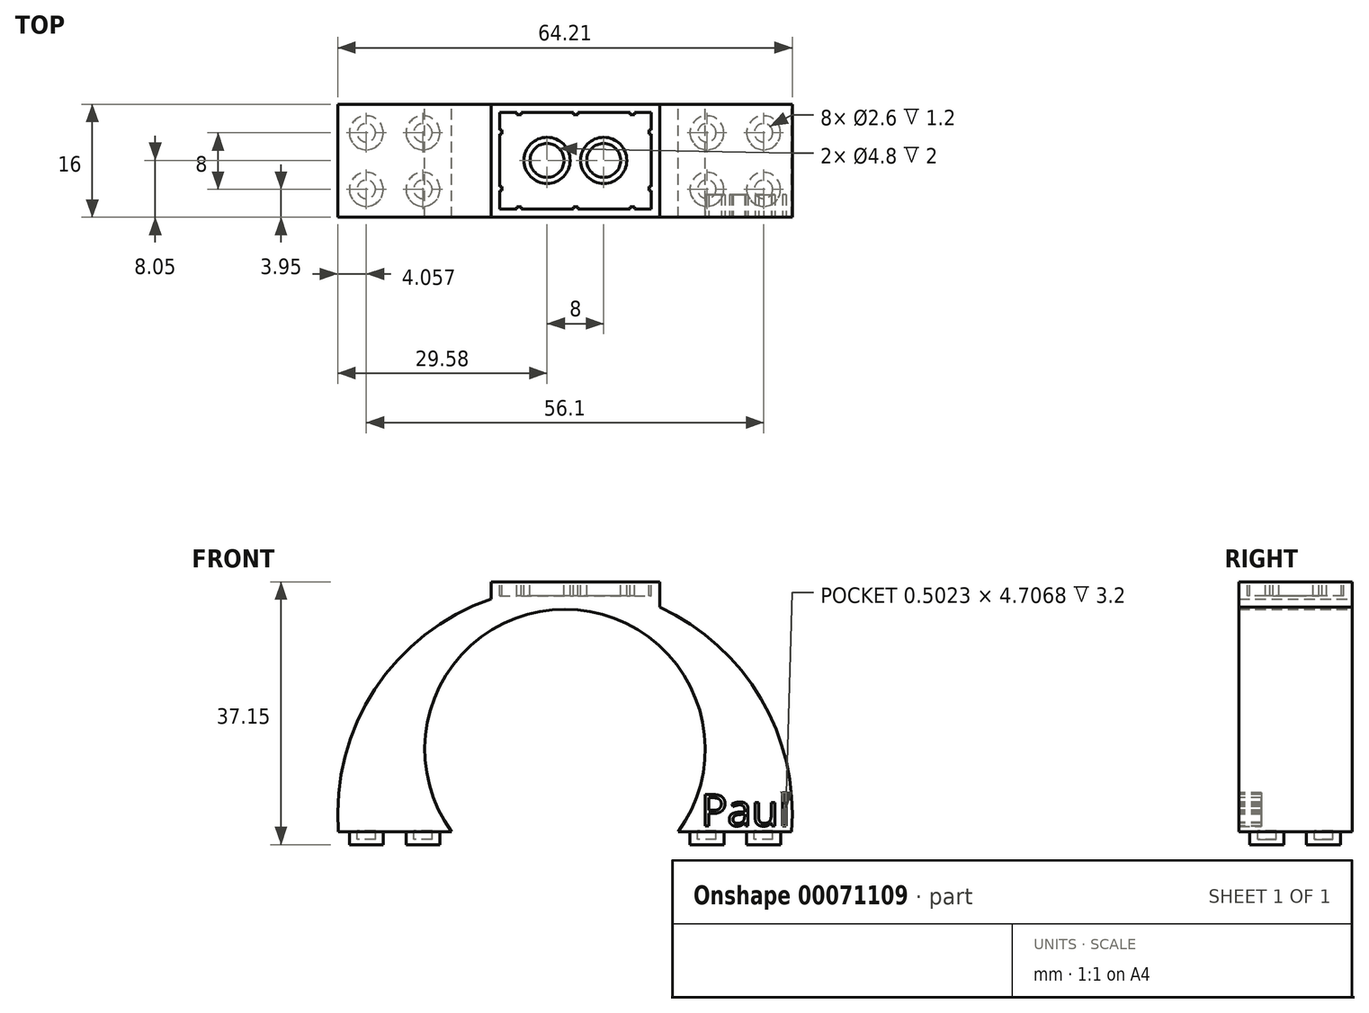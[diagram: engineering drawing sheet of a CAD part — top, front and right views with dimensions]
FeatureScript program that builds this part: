
annotation { "Feature Type Name" : "Feature", "Feature Type Description" : "" }
export const myFeature = defineFeature(function(context is Context, id is Id, definition is map)
    precondition{}
    {
        {
            var Q0;
            Q0=qCreatedBy(makeId("Front.planeOp"),FACE);
            var sketch = newSketch(context, id + "F0", { "sketchPlane" : qUnion([Q0])});
            skLineSegment(sketch, "E0.bottom", {"start": v(-33.47, 63.85) * mm, "end": v(30.53, 63.85) * mm, "construction": true});
            skLineSegment(sketch, "E0.top", {"start": v(-33.47, -0.15) * mm, "end": v(30.53, -0.15) * mm, "construction": true});
            skLineSegment(sketch, "E0.left", {"start": v(-33.47, 63.85) * mm, "end": v(-33.47, -0.15) * mm, "construction": true});
            skLineSegment(sketch, "E0.right", {"start": v(30.53, 63.85) * mm, "end": v(30.53, -0.15) * mm, "construction": true});
            skArc(sketch, "E1", {"start": v(14.53, -0.15) * mm, "mid": v(-1.47, 31.32) * mm, "end": v(-17.47, -0.15) * mm});
            skLineSegment(sketch, "E2", {"start": v(-33.47, -0.15) * mm, "end": v(-17.47, -0.15) * mm});
            skLineSegment(sketch, "E3", {"start": v(14.53, -0.15) * mm, "end": v(30.53, -0.15) * mm});
            skArc(sketch, "E4", {"start": v(30.53, -0.15) * mm, "mid": v(-1.47, 34.52) * mm, "end": v(-33.47, -0.15) * mm});
            skSolve(sketch);
        }
        {
            var Q0;
            Q0 = qSketchRegion(id + "F0", true);
            extrude(context, id + "F1", {"entities" : qUnion([Q0]), "depth" : 16 * mm});
        }
        {
            var Q0;
            Q0=makeQuery(id+"F1.opExtrude","SWEPT_FACE",FACE,{"disambiguationData":[OSD([sQuery(id+"F0.wireOp",EDGE,"E2")])]});
            var sketch = newSketch(context, id + "F2", { "sketchPlane" : qUnion([Q0])});
            skLineSegment(sketch, "E5", {"start": v(-45.71, 8) * mm, "end": v(-17.47, 8) * mm, "construction": true});
            skPoint(sketch, "E5.startSnap0", {"position": v(-17.47, 8) * mm});
            skCircle(sketch, "E6", {"center": v(-29.52, 12.05) * mm, "radius": 2.4 * mm});
            skCircle(sketch, "E7.0.1.0", {"center": v(-29.52, 4.05) * mm, "radius": 2.4 * mm});
            skCircle(sketch, "E7.1.0.0", {"center": v(-21.52, 12.05) * mm, "radius": 2.4 * mm});
            skCircle(sketch, "E7.1.1.0", {"center": v(-21.52, 4.05) * mm, "radius": 2.4 * mm});
            skLineSegment(sketch, "E7.direction1", {"start": v(-29.52, 12.05) * mm, "end": v(-21.52, 12.05) * mm, "construction": true});
            skLineSegment(sketch, "E7.direction2", {"start": v(-29.52, 12.05) * mm, "end": v(-29.52, 4.05) * mm, "construction": true});
            skLineSegment(sketch, "E8", {"start": v(-17.47, 8) * mm, "end": v(43.86, 8) * mm, "construction": true});
            skCircle(sketch, "E9", {"center": v(26.58, 12.05) * mm, "radius": 2.4 * mm});
            skCircle(sketch, "E10.0.1.0", {"center": v(26.58, 4.05) * mm, "radius": 2.4 * mm});
            skCircle(sketch, "E10.1.0.0", {"center": v(18.58, 12.05) * mm, "radius": 2.4 * mm});
            skCircle(sketch, "E10.1.1.0", {"center": v(18.58, 4.05) * mm, "radius": 2.4 * mm});
            skLineSegment(sketch, "E10.direction1", {"start": v(26.58, 12.05) * mm, "end": v(18.58, 12.05) * mm, "construction": true});
            skLineSegment(sketch, "E10.direction2", {"start": v(26.58, 12.05) * mm, "end": v(26.58, 4.05) * mm, "construction": true});
            skSolve(sketch);
        }
        {
            var Q0;
            Q0 = qSketchRegion(id + "F2", true);
            extrude(context, id + "F3", {"entities" : qUnion([Q0]), "operationType" : NewBodyOperationType.ADD, "depth" : 1.8 * mm});
        }
        {
            var Q0;
            Q0=qCreatedBy(makeId("Top.planeOp"),FACE);
            var sketch = newSketch(context, id + "F4", { "sketchPlane" : qUnion([Q0])});
            skCircle(sketch, "E11", {"center": v(-29.52, -4.05) * mm, "radius": 1.3 * mm});
            skCircle(sketch, "E12.0.1.0", {"center": v(-29.52, -12.05) * mm, "radius": 1.3 * mm});
            skCircle(sketch, "E12.1.0.0", {"center": v(-21.52, -4.05) * mm, "radius": 1.3 * mm});
            skCircle(sketch, "E12.1.1.0", {"center": v(-21.52, -12.05) * mm, "radius": 1.3 * mm});
            skLineSegment(sketch, "E12.direction1", {"start": v(-29.52, -4.05) * mm, "end": v(-21.52, -4.05) * mm, "construction": true});
            skLineSegment(sketch, "E12.direction2", {"start": v(-29.52, -4.05) * mm, "end": v(-29.52, -12.05) * mm, "construction": true});
            skSolve(sketch);
        }
        {
            var Q0;
            Q0 = qSketchRegion(id + "F4", true);
            extrude(context, id + "F5", {"entities" : qUnion([Q0]), "operationType" : NewBodyOperationType.REMOVE, "oppositeDirection" : true, "depth" : 1.2 * mm});
        }
        {
            var Q0;
            Q0=qCreatedBy(makeId("Top.planeOp"),FACE);
            var sketch = newSketch(context, id + "F6", { "sketchPlane" : qUnion([Q0])});
            skCircle(sketch, "E13", {"center": v(18.58, -4.05) * mm, "radius": 1.3 * mm});
            skCircle(sketch, "E14.0.1.0", {"center": v(18.58, -12.05) * mm, "radius": 1.3 * mm});
            skCircle(sketch, "E14.1.0.0", {"center": v(26.58, -4.05) * mm, "radius": 1.3 * mm});
            skCircle(sketch, "E14.1.1.0", {"center": v(26.58, -12.05) * mm, "radius": 1.3 * mm});
            skLineSegment(sketch, "E14.direction1", {"start": v(18.58, -4.05) * mm, "end": v(26.58, -4.05) * mm, "construction": true});
            skLineSegment(sketch, "E14.direction2", {"start": v(18.58, -4.05) * mm, "end": v(18.58, -12.05) * mm, "construction": true});
            skSolve(sketch);
        }
        {
            var Q0;
            Q0 = qSketchRegion(id + "F6", true);
            extrude(context, id + "F7", {"entities" : qUnion([Q0]), "operationType" : NewBodyOperationType.REMOVE, "oppositeDirection" : true, "depth" : 1.2 * mm});
        }
        {
            var Q0;
            Q0=qCreatedBy(makeId("Top.planeOp"),FACE);
            cPlane(context, id + "F8", {"entities" : qUnion([Q0]), "cplaneType" : CPlaneType.OFFSET, "offset" : 32 * mm, "width" : 150 * mm, "height" : 150 * mm});
        }
        {
            var Q0;
            Q0=qCreatedBy(id+"F8.planeOp",FACE);
            var sketch = newSketch(context, id + "F9", { "sketchPlane" : qUnion([Q0])});
            skLineSegment(sketch, "E15.bottom", {"start": v(-11.9, 0) * mm, "end": v(11.9, 0) * mm});
            skLineSegment(sketch, "E15.top", {"start": v(-11.9, -16) * mm, "end": v(11.9, -16) * mm});
            skLineSegment(sketch, "E15.left", {"start": v(-11.9, 0) * mm, "end": v(-11.9, -16) * mm});
            skLineSegment(sketch, "E15.right", {"start": v(11.9, 0) * mm, "end": v(11.9, -16) * mm});
            skSolve(sketch);
        }
        {
            var Q0;
            Q0 = qSketchRegion(id + "F9", true);
            extrude(context, id + "F10", {"entities" : qUnion([Q0]), "operationType" : NewBodyOperationType.ADD, "depth" : 3.2 * mm});
        }
        {
            var Q0;
            Q0 = qSketchRegion(id + "F9", true);
            extrude(context, id + "F11", {"entities" : qUnion([Q0]), "operationType" : NewBodyOperationType.ADD, "oppositeDirection" : true, "depth" : .5 * mm});
        }
        {
            var Q0;
            Q0=makeQuery(id+"F10.opExtrude","CAP_FACE",FACE,{"disambiguationData":[OSD([sQuery(id+"F9.wireOp",EDGE,"E15.bottom"),sQuery(id+"F9.wireOp",EDGE,"E15.top"),sQuery(id+"F9.wireOp",EDGE,"E15.left"),sQuery(id+"F9.wireOp",EDGE,"E15.right")])],"isStart":false});
            var sketch = newSketch(context, id + "F12", { "sketchPlane" : qUnion([Q0])});
            skCircle(sketch, "E16", {"center": v(0, -3.95) * mm, "radius": 2.4 * mm, "construction": true});
            skCircle(sketch, "E17.1.0.0", {"center": v(8, -3.95) * mm, "radius": 2.4 * mm, "construction": true});
            skLineSegment(sketch, "E17.direction1", {"start": v(0, -3.95) * mm, "end": v(8, -3.95) * mm, "construction": true});
            skLineSegment(sketch, "E17.direction2", {"start": v(0, -3.95) * mm, "end": v(0, -11.95) * mm, "construction": true});
            skCircle(sketch, "E18", {"center": v(-8, -3.95) * mm, "radius": 2.4 * mm, "construction": true});
            skCircle(sketch, "E19.0.0.1", {"center": v(0, -11.95) * mm, "radius": 2.4 * mm, "construction": true});
            skCircle(sketch, "E19.0.1.1", {"center": v(8, -11.95) * mm, "radius": 2.4 * mm, "construction": true});
            skCircle(sketch, "E20.0.1.0", {"center": v(-8, -11.95) * mm, "radius": 2.4 * mm, "construction": true});
            skLineSegment(sketch, "E20.direction1", {"start": v(-8, -3.95) * mm, "end": v(-14.17, -3.95) * mm, "construction": true});
            skLineSegment(sketch, "E20.direction2", {"start": v(-8, -3.95) * mm, "end": v(-8, -11.95) * mm, "construction": true});
            skLineSegment(sketch, "E21", {"start": v(-8, -3.95) * mm, "end": v(0, -11.95) * mm, "construction": true});
            skLineSegment(sketch, "E22", {"start": v(0, -3.95) * mm, "end": v(-8, -11.95) * mm, "construction": true});
            skLineSegment(sketch, "E23", {"start": v(0, -3.95) * mm, "end": v(8, -11.95) * mm, "construction": true});
            skLineSegment(sketch, "E24", {"start": v(8, -3.95) * mm, "end": v(0, -11.95) * mm, "construction": true});
            skPoint(sketch, "E25", {"position": v(-4, -7.95) * mm});
            skPoint(sketch, "E26", {"position": v(4, -7.95) * mm});
            skCircle(sketch, "E27", {"center": v(-4, -7.95) * mm, "radius": 2.4 * mm});
            skCircle(sketch, "E28", {"center": v(-4, -7.95) * mm, "radius": 3.25 * mm});
            skCircle(sketch, "E29", {"center": v(4, -7.95) * mm, "radius": 2.4 * mm});
            skCircle(sketch, "E30", {"center": v(4, -7.95) * mm, "radius": 3.25 * mm});
            skSolve(sketch);
        }
        {
            var Q0;
            Q0=makeQuery(id+"F12.imprint","IMPRINT",FACE,{"disambiguationData":[TD([[makeQuery(id+"F12.imprint","IMPRINT",EDGE,{"derivedFrom":sQuery(id+"F12.wireOp",EDGE,"E28")}),-1.0]])]});
            var sketch = newSketch(context, id + "F13", { "sketchPlane" : qUnion([Q0])});
            skLineSegment(sketch, "E31.bottom", {"start": v(-10.7, -1.2) * mm, "end": v(10.7, -1.2) * mm});
            skLineSegment(sketch, "E31.top", {"start": v(-10.7, -14.8) * mm, "end": v(10.7, -14.8) * mm});
            skLineSegment(sketch, "E31.left", {"start": v(-10.7, -1.2) * mm, "end": v(-10.7, -14.8) * mm});
            skLineSegment(sketch, "E31.right", {"start": v(10.7, -1.2) * mm, "end": v(10.7, -14.8) * mm});
            skSolve(sketch);
        }
        {
            var Q0;
            Q0 = qSketchRegion(id + "F13", true);
            extrude(context, id + "F14", {"entities" : qUnion([Q0]), "operationType" : NewBodyOperationType.REMOVE, "oppositeDirection" : true, "depth" : 2 * mm});
        }
        {
            var Q0;
            Q0 = qSketchRegion(id + "F12", true);
            extrude(context, id + "F15", {"entities" : qUnion([Q0]), "operationType" : NewBodyOperationType.ADD, "oppositeDirection" : true, "depth" : 3.2 * mm});
        }
        {
            var Q0;
            Q0=makeQuery(id+"F10.opExtrude","CAP_FACE",FACE,{"disambiguationData":[OSD([sQuery(id+"F9.wireOp",EDGE,"E15.bottom"),sQuery(id+"F9.wireOp",EDGE,"E15.top"),sQuery(id+"F9.wireOp",EDGE,"E15.left"),sQuery(id+"F9.wireOp",EDGE,"E15.right")])],"isStart":false});
            var sketch = newSketch(context, id + "F16", { "sketchPlane" : qUnion([Q0])});
            skLineSegment(sketch, "E32.bottom", {"start": v(-7.65, -1.2) * mm, "end": v(-8.25, -1.2) * mm});
            skLineSegment(sketch, "E32.top", {"start": v(-7.65, -1.5) * mm, "end": v(-8.25, -1.5) * mm});
            skLineSegment(sketch, "E32.left", {"start": v(-7.65, -1.2) * mm, "end": v(-7.65, -1.5) * mm});
            skLineSegment(sketch, "E32.right", {"start": v(-8.25, -1.2) * mm, "end": v(-8.25, -1.5) * mm});
            skLineSegment(sketch, "E33", {"start": v(-7.95, -11.93) * mm, "end": v(-7.95, 1.87) * mm, "construction": true});
            skLineSegment(sketch, "E34.0.1.0", {"start": v(-7.65, -14.5) * mm, "end": v(-8.25, -14.5) * mm});
            skLineSegment(sketch, "E34.0.1.1", {"start": v(-7.65, -14.8) * mm, "end": v(-8.25, -14.8) * mm});
            skLineSegment(sketch, "E34.0.1.2", {"start": v(-7.65, -14.5) * mm, "end": v(-7.65, -14.8) * mm});
            skLineSegment(sketch, "E34.0.1.3", {"start": v(-8.25, -14.5) * mm, "end": v(-8.25, -14.8) * mm});
            skLineSegment(sketch, "E34.1.0.0", {"start": v(0.35, -1.2) * mm, "end": v(-0.25, -1.2) * mm});
            skLineSegment(sketch, "E34.1.0.1", {"start": v(0.35, -1.5) * mm, "end": v(-0.25, -1.5) * mm});
            skLineSegment(sketch, "E34.1.0.2", {"start": v(0.35, -1.2) * mm, "end": v(0.35, -1.5) * mm});
            skLineSegment(sketch, "E34.1.0.3", {"start": v(-0.25, -1.2) * mm, "end": v(-0.25, -1.5) * mm});
            skLineSegment(sketch, "E34.1.1.0", {"start": v(0.35, -14.5) * mm, "end": v(-0.25, -14.5) * mm});
            skLineSegment(sketch, "E34.1.1.1", {"start": v(0.35, -14.8) * mm, "end": v(-0.25, -14.8) * mm});
            skLineSegment(sketch, "E34.1.1.2", {"start": v(0.35, -14.5) * mm, "end": v(0.35, -14.8) * mm});
            skLineSegment(sketch, "E34.1.1.3", {"start": v(-0.25, -14.5) * mm, "end": v(-0.25, -14.8) * mm});
            skLineSegment(sketch, "E34.2.0.0", {"start": v(8.35, -1.2) * mm, "end": v(7.75, -1.2) * mm});
            skLineSegment(sketch, "E34.2.0.1", {"start": v(8.35, -1.5) * mm, "end": v(7.75, -1.5) * mm});
            skLineSegment(sketch, "E34.2.0.2", {"start": v(8.35, -1.2) * mm, "end": v(8.35, -1.5) * mm});
            skLineSegment(sketch, "E34.2.0.3", {"start": v(7.75, -1.2) * mm, "end": v(7.75, -1.5) * mm});
            skLineSegment(sketch, "E34.2.1.0", {"start": v(8.35, -14.5) * mm, "end": v(7.75, -14.5) * mm});
            skLineSegment(sketch, "E34.2.1.1", {"start": v(8.35, -14.8) * mm, "end": v(7.75, -14.8) * mm});
            skLineSegment(sketch, "E34.2.1.2", {"start": v(8.35, -14.5) * mm, "end": v(8.35, -14.8) * mm});
            skLineSegment(sketch, "E34.2.1.3", {"start": v(7.75, -14.5) * mm, "end": v(7.75, -14.8) * mm});
            skLineSegment(sketch, "E34.direction1", {"start": v(-8.25, -1.2) * mm, "end": v(-0.25, -1.2) * mm, "construction": true});
            skLineSegment(sketch, "E34.direction2", {"start": v(-8.25, -1.2) * mm, "end": v(-8.25, -14.5) * mm, "construction": true});
            skSolve(sketch);
        }
        {
            var Q0;
            Q0 = qSketchRegion(id + "F16", true);
            var Q1;
            Q1=makeQuery(id+"F10.opExtrude","CAP_FACE",FACE,{"disambiguationData":[OSD([sQuery(id+"F9.wireOp",EDGE,"E15.bottom"),sQuery(id+"F9.wireOp",EDGE,"E15.top"),sQuery(id+"F9.wireOp",EDGE,"E15.left"),sQuery(id+"F9.wireOp",EDGE,"E15.right")])],"isStart":false});
            extrude(context, id + "F17", {"entities" : qUnion([Q0]), "operationType" : NewBodyOperationType.ADD, "oppositeDirection" : true, "endBoundEntityFace" : qUnion([Q1]), "depth" : 3.2 * mm});
        }
        {
            var Q0;
            Q0=makeQuery(id+"F12.imprint","IMPRINT",FACE,{"disambiguationData":[TD([[makeQuery(id+"F12.imprint","IMPRINT",EDGE,{"derivedFrom":sQuery(id+"F12.wireOp",EDGE,"E28")}),-1.0]])]});
            var sketch = newSketch(context, id + "F18", { "sketchPlane" : qUnion([Q0])});
            skLineSegment(sketch, "E35.bottom", {"start": v(-10.4, -3.65) * mm, "end": v(-10.7, -3.65) * mm});
            skLineSegment(sketch, "E35.top", {"start": v(-10.4, -4.25) * mm, "end": v(-10.7, -4.25) * mm});
            skLineSegment(sketch, "E35.left", {"start": v(-10.4, -3.65) * mm, "end": v(-10.4, -4.25) * mm});
            skLineSegment(sketch, "E35.right", {"start": v(-10.7, -3.65) * mm, "end": v(-10.7, -4.25) * mm});
            skLineSegment(sketch, "E36.0.1.0", {"start": v(-10.4, -12.25) * mm, "end": v(-10.7, -12.25) * mm});
            skLineSegment(sketch, "E36.0.1.1", {"start": v(-10.7, -11.65) * mm, "end": v(-10.7, -12.25) * mm});
            skLineSegment(sketch, "E36.0.1.2", {"start": v(-10.4, -11.65) * mm, "end": v(-10.4, -12.25) * mm});
            skLineSegment(sketch, "E36.0.1.3", {"start": v(-10.4, -11.65) * mm, "end": v(-10.7, -11.65) * mm});
            skLineSegment(sketch, "E36.1.0.0", {"start": v(10.7, -4.25) * mm, "end": v(10.4, -4.25) * mm});
            skLineSegment(sketch, "E36.1.0.1", {"start": v(10.4, -3.65) * mm, "end": v(10.4, -4.25) * mm});
            skLineSegment(sketch, "E36.1.0.2", {"start": v(10.7, -3.65) * mm, "end": v(10.7, -4.25) * mm});
            skLineSegment(sketch, "E36.1.0.3", {"start": v(10.7, -3.65) * mm, "end": v(10.4, -3.65) * mm});
            skLineSegment(sketch, "E36.1.1.0", {"start": v(10.7, -12.25) * mm, "end": v(10.4, -12.25) * mm});
            skLineSegment(sketch, "E36.1.1.1", {"start": v(10.4, -11.65) * mm, "end": v(10.4, -12.25) * mm});
            skLineSegment(sketch, "E36.1.1.2", {"start": v(10.7, -11.65) * mm, "end": v(10.7, -12.25) * mm});
            skLineSegment(sketch, "E36.1.1.3", {"start": v(10.7, -11.65) * mm, "end": v(10.4, -11.65) * mm});
            skLineSegment(sketch, "E36.direction1", {"start": v(-10.7, -4.25) * mm, "end": v(10.4, -4.25) * mm, "construction": true});
            skLineSegment(sketch, "E36.direction2", {"start": v(-10.7, -4.25) * mm, "end": v(-10.7, -12.25) * mm, "construction": true});
            skSolve(sketch);
        }
        {
            var Q0;
            Q0 = qSketchRegion(id + "F18", true);
            extrude(context, id + "F19", {"entities" : qUnion([Q0]), "operationType" : NewBodyOperationType.ADD, "oppositeDirection" : true, "depth" : 3.2 * mm});
        }
        {
            var Q0;
            {var subQ0=sQuery(id+"F9.wireOp",EDGE,"E15.top");Q0=makeQuery(id+"F11.boolean.opBoolean","MERGE",FACE,{"derivedFrom":[makeQuery(id+"F10.boolean.opBoolean","MERGE",FACE,{"derivedFrom":[makeQuery(id+"F1.opExtrude","CAP_FACE",FACE,{"disambiguationData":[OSD([sQuery(id+"F0.wireOp",EDGE,"E1"),sQuery(id+"F0.wireOp",EDGE,"E2"),sQuery(id+"F0.wireOp",EDGE,"E3"),sQuery(id+"F0.wireOp",EDGE,"E4")])],"isStart":false}),makeQuery(id+"F10.opExtrude","SWEPT_FACE",FACE,{"disambiguationData":[OSD([subQ0])]})]}),makeQuery(id+"F11.opExtrude","SWEPT_FACE",FACE,{"disambiguationData":[OSD([subQ0])]})]});}
            var sketch = newSketch(context, id + "F20", { "sketchPlane" : qUnion([Q0])});
            skText(sketch, "E37", { "text": "Paul", "fontName": "OpenSans-Regular.ttf"});
            const initialGuessF20  = {"E37": [0.01772, 0.0007, 1, 0, 0.00446]};
            skSetInitialGuess(sketch, initialGuessF20);
            skSolve(sketch);
        }
        {
            var Q0;
            Q0 = qSketchRegion(id + "F20", true);
            extrude(context, id + "F21", {"entities" : qUnion([Q0]), "operationType" : NewBodyOperationType.REMOVE, "oppositeDirection" : true, "depth" : 3.2 * mm});
        }
    });
